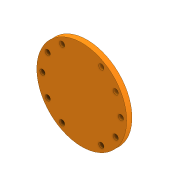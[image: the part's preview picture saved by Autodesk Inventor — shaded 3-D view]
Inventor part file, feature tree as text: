
AUTODESK INVENTOR PART (.ipt)
format: ipt  version: 2020 (Build 240168000, 168)  size: 659,968 bytes
history: native  units: in
note: dims shown in document units (in); Inventor stores cm internally (conversion verified against a paired STEP export)
features: chamfer x35, sketch x24, extrude x21, plane x9, projected_geometry x4, revolve x1, fillet x1, emboss x1
ambient origin geometry x8: Origin, YZ Plane, XZ Plane, XY Plane, X Axis, Y Axis, Z Axis, Center Point
bodies: Solid1 (feature_tree)
feature tree (96):
  extrude  "Extrusion1"  Depth=0.315in TaperAngle=0.0deg
  chamfer  "Chamfer1"  Distance=0.315in
  extrude  "Extrusion2"  Depth=2.3622in TaperAngle=360.0deg
  extrude  "Extrusion3"  Depth=0.0197in TaperAngle=0.0deg
  extrude  "Extrusion4"  Depth=0.1575in TaperAngle=0.0deg
  extrude  "Extrusion5"  Depth=0.1575in TaperAngle=0.0deg
  revolve  "Revolution1"  [1 undecoded]
  plane  "Work Plane1"
  extrude  "Extrusion6"  Depth=0.1575in
  plane  "Work Plane2"
  plane  "Work Plane3"
  extrude  "Extrusion8"  [1 undecoded]
  extrude  "Extrusion9"  Depth=0.1575in TaperAngle=0.0deg
  chamfer  "Chamfer3"  Distance=1.8898in
  extrude  "Extrusion10"  Depth=1.8898in
  plane  "Work Plane4"
  extrude  "Extrusion11"  Depth=0.315in TaperAngle=0.0deg
  extrude  "Extrusion12"  Depth=0.2756in
  extrude  "Extrusion13"  Depth=3.1496in TaperAngle=360.0deg
  chamfer  "Chamfer4"  Distance=0.2756in
  chamfer  "Chamfer5"  Distance=0.9843in
  chamfer  "Chamfer6"  Distance=0.315in
  chamfer  "Chamfer7"  Distance=3.937in Angle=360.0deg
  chamfer  "Chamfer8"  Distance=0.315in
  chamfer  "Chamfer9"  Distance=0.315in
  chamfer  "Chamfer10"  Distance=0.315in
  chamfer  "Chamfer11"  Distance=0.315in
  chamfer  "Chamfer12"  Distance=0.315in
  chamfer  "Chamfer13"  Distance=0.315in
  chamfer  "Chamfer14"  Distance=0.315in
  chamfer  "Chamfer15"  Distance=0.315in
  chamfer  "Chamfer16"  Distance=0.315in
  chamfer  "Chamfer17"  Distance=0.315in
  chamfer  "Chamfer18"  Distance=0.315in
  chamfer  "Chamfer19"  Distance=0.315in
  chamfer  "Chamfer20"  Distance=0.315in
  chamfer  "Chamfer21"  Distance=0.315in
  chamfer  "Chamfer22"  Distance=0.315in
  chamfer  "Chamfer23"  Distance=0.315in
  chamfer  "Chamfer24"  Distance=0.315in
  chamfer  "Chamfer25"  Distance=0.315in
  chamfer  "Chamfer26"  Distance=0.315in
  chamfer  "Chamfer27"  Distance=0.315in
  chamfer  "Chamfer28"  Distance=0.315in
  chamfer  "Chamfer29"  Distance=0.315in
  chamfer  "Chamfer30"  Distance=0.315in
  chamfer  "Chamfer31"  Distance=0.315in
  chamfer  "Chamfer32"  Distance=0.315in
  chamfer  "Chamfer33"  Distance=0.315in
  plane  "Work Plane5"
  extrude  "Extrusion15"  Depth=0.315in
  extrude  "Extrusion16"  Depth=0.315in
  plane  "Work Plane6"
  extrude  "Extrusion18"  Depth=0.9843in
  extrude  "Extrusion20"  TaperAngle=60.0deg  [1 undecoded]
  extrude  "Extrusion21"  TaperAngle=0.0deg  [1 undecoded]
  extrude  "Extrusion22"  Depth=0.1575in TaperAngle=0.0deg
  chamfer  "Chamfer34"  Distance=0.315in
  chamfer  "Chamfer35"  Distance=0.2067in
  fillet  "Fillet1"  Radius=0.0787in
  plane  "Work Plane7"
  emboss  "Emboss1"
  chamfer  "Chamfer36"  Angle=45.0deg  [1 undecoded]
  sketch  "Sketch25"  dims[d162=0.315in d163=0.125in d164=0.0137in d166=0.9843in]
  plane  "Work Plane8"
  plane  "Work Plane9"
  extrude  "Extrusion23"  Depth=0.1575in TaperAngle=0.0deg
  extrude  "Extrusion24"  [1 undecoded]
  extrude  "Extrusion25"  Depth=0.1575in TaperAngle=0.0deg
  sketch  "Sketch1"  dims[d0=0.4724in d1=0.315in d2=0.0in d3=0.315in d4=0.125in d5=0.0137in]
  sketch  "Sketch2"  dims[d6=0.0157in d7=2.3622in d9=360.0deg]
  sketch  "Sketch3"  dims[d11=0.315in d12=0.0in d13=0.0197in d14=0.0in]
  projected_geometry  "Projected Loop1"
  sketch  "Sketch4"  dims[d15=2.5591in d16=0.1575in d17=0.0in]
  sketch  "Sketch5"  dims[d18=0.1575in d19=1.2598in d20=0.0in]
  sketch  "Sketch6"  dims[d21=1.1024in d22=0.5512in]
  sketch  "Sketch7"  dims[d23=0.8465in d24=0.1575in]
  sketch  "Sketch9"  dims[d25=90.0deg d26=-2.1063in]
  sketch  "Sketch10"  dims[d27=0.1575in d28=0.1575in d29=0.0in d33=-0.1575in d41=1.8898in]
  sketch  "Sketch11"  dims[d42=1.2795in d43=1.8898in]
  sketch  "Sketch12"  dims[d44=0.2165in d45=0.315in d46=0.0in]
  sketch  "Sketch13"  dims[d47=1.1811in d48=0.0in d49=0.2756in d50=0.125in d51=0.0137in]
  sketch  "Sketch14"  dims[d52=0.0157in d53=3.1496in d55=360.0deg d57=0.2756in d58=0.0in]
  sketch  "Sketch16"  dims[d59=-0.2756in d61=0.9843in d62=0.0in]
  sketch  "Sketch17"  dims[d63=0.4764in d64=0.315in d65=0.0in]
  sketch  "Sketch19"  dims[d66=0.0787in]
  projected_geometry  "Projected Loop2"
  projected_geometry  "Projected Loop3"
  sketch  "Sketch21"  dims[d67=0.0787in]
  sketch  "Sketch22"  dims[d68=0.0394in d69=3.937in d71=360.0deg d73=0.315in d74=0.0in d75=0.315in d76=0.125in d77=0.0137in d78=0.315in d79=0.125in d80=0.0137in d81=0.315in d82=0.125in d83=0.0137in d84=0.315in d85=0.125in d86=0.0137in d87=0.315in d88=0.125in d89=0.0137in d90=0.315in d91=0.125in d92=0.0137in d93=0.315in d94=0.125in d95=0.0137in d96=0.315in d97=0.125in d98=0.0137in d99=0.315in d100=0.125in d101=0.0137in d102=0.315in d103=0.125in d104=0.0137in d105=0.315in d106=0.125in d107=0.0137in d108=0.315in d109=0.125in d110=0.0137in d111=0.315in d112=0.125in d113=0.0137in d114=0.315in d115=0.125in d116=0.0137in d117=0.315in d118=0.125in d119=0.0137in d120=0.315in d121=0.125in d122=0.0137in d123=0.315in d124=0.125in d125=0.0137in d126=0.315in d127=0.125in d128=0.0137in d129=0.315in d130=0.125in d131=0.0137in d132=0.315in d133=0.125in d134=0.0137in d135=0.315in d136=0.125in d137=0.0137in d138=0.315in d139=0.125in d140=0.0137in d141=0.315in d142=0.125in d143=0.0137in d144=0.315in d145=0.125in d146=0.0137in d147=0.315in d148=0.125in d149=0.0137in]
  sketch  "Sketch23"  dims[d150=0.315in d151=0.125in d152=0.0137in d153=0.315in d154=0.125in d155=0.0137in]
  projected_geometry  "Projected Loop4"
  sketch  "Sketch24"  dims[d156=0.315in d157=0.125in d158=0.0137in d159=0.315in d160=0.125in d161=0.0137in]
  sketch  "Sketch28"  dims[d171=-0.2756in d172=60.0deg]
  sketch  "Sketch29"  dims[d173=60.0deg d174=0.0in]
  sketch  "Sketch30"  dims[d175=0.0in d176=2.3622in d177=0.0in d178=0.315in d179=0.2067in d180=0.0787in d181=45.0deg d182=0.1969in d183=0.0in d187=-0.4921in d188=0.1969in d189=0.0in d193=0.315in d194=0.0984in d195=0.0in d196=0.2362in d197=0.0984in d198=0.0in d199=0.0984in d200=0.0in d201=0.0591in d202=0.125in d203=0.0137in d204=0.0591in d205=0.125in d206=0.0137in d207=0.0197in d209=0.0394in d210=0.0in d211=0.0787in d212=0.125in d213=0.0137in d214=2.126in d215=-0.1575in d217=-0.1575in d218=0.157in d219=0.0in d221=0.1083in d222=0.1575in d223=4.7244in d225=360.0deg d227=1.0in d228=0.0in d229=0.0622in d230=1.0in d231=0.0in]
note: 6 required parameter values undecoded (feature->parameter linkage not recoverable at this tier; creation-order binding heuristic only, values carry confidence <= 0.55)